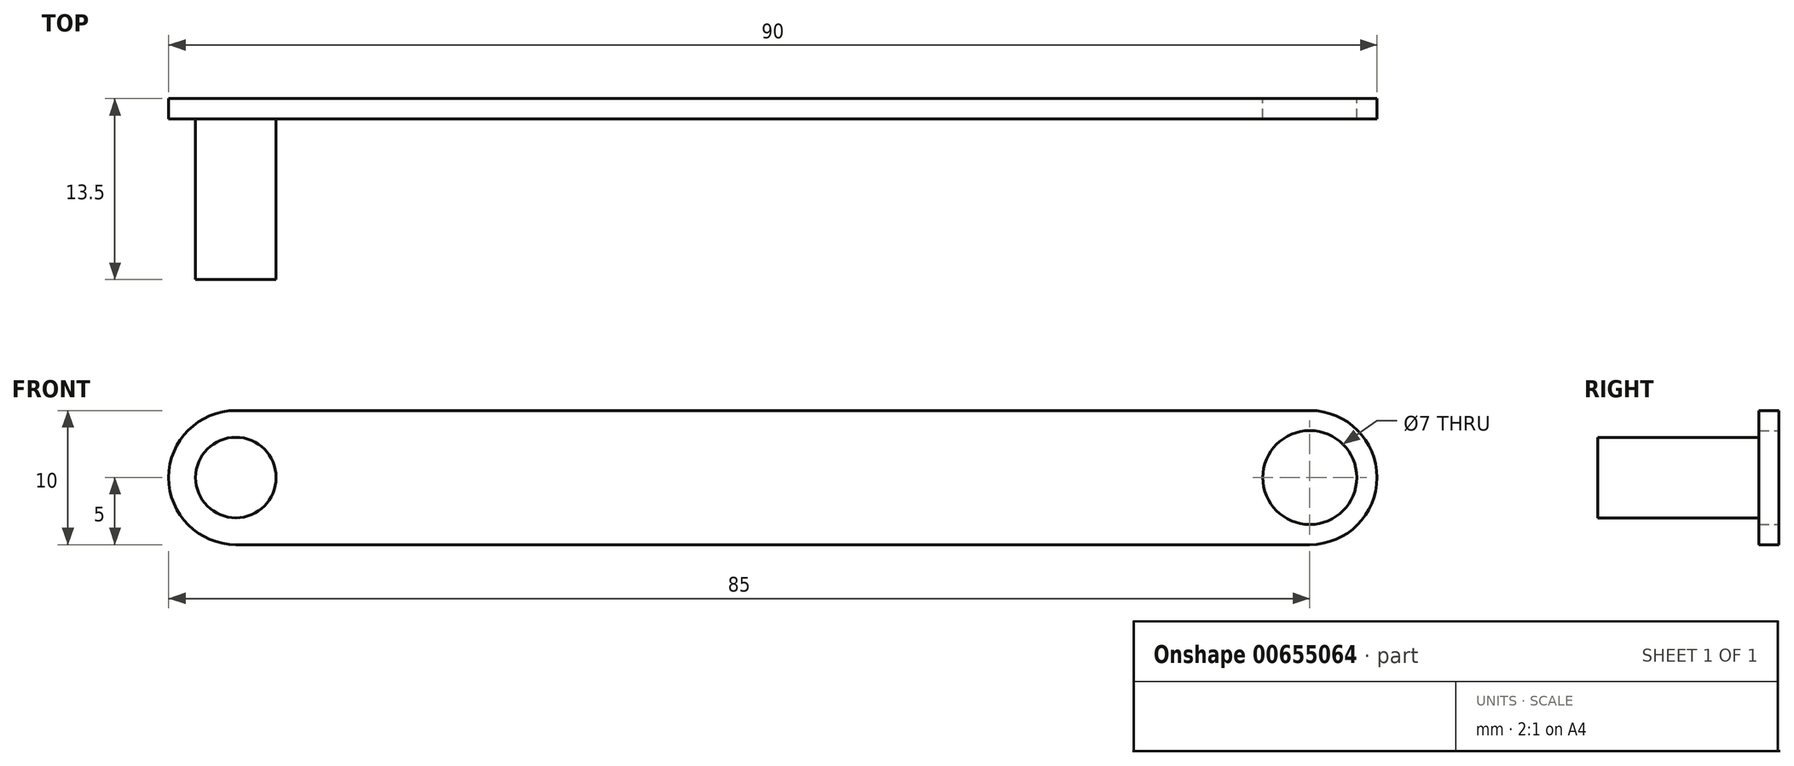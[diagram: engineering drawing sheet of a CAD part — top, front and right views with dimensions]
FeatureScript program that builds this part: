
annotation { "Feature Type Name" : "Feature", "Feature Type Description" : "" }
export const myFeature = defineFeature(function(context is Context, id is Id, definition is map)
    precondition{}
    {
        {
            var Q0;
            Q0=qCreatedBy(makeId("Front.planeOp"),FACE);
            var sketch = newSketch(context, id + "F0", { "sketchPlane" : qUnion([Q0])});
            skArc(sketch, "E0", {"start": v(0, 5) * mm, "mid": v(-5, 0) * mm, "end": v(0, -5) * mm});
            skArc(sketch, "E1.1.0.0", {"start": v(80, -5) * mm, "mid": v(85, 0) * mm, "end": v(80, 5) * mm});
            skCircle(sketch, "E1.1.0.1", {"center": v(80, 0) * mm, "radius": 3.5 * mm});
            skLineSegment(sketch, "E2", {"start": v(0, 5) * mm, "end": v(80, 5) * mm});
            skLineSegment(sketch, "E3", {"start": v(0, -5) * mm, "end": v(80, -5) * mm});
            skSolve(sketch);
        }
        {
            var Q0;
            Q0 = qSketchRegion(id + "F0", true);
            extrude(context, id + "F1", {"entities" : qUnion([Q0]), "depth" : 1.5 * mm, "offsetDistance" : 25 * mm});
        }
        {
            var Q0;
            Q0=makeQuery(id+"F1.opExtrude","CAP_FACE",FACE,{"disambiguationData":[OSD([sQuery(id+"F0.wireOp",EDGE,"E0"),sQuery(id+"F0.wireOp",EDGE,"E1.1.0.0"),sQuery(id+"F0.wireOp",EDGE,"E1.1.0.1"),sQuery(id+"F0.wireOp",EDGE,"E2"),sQuery(id+"F0.wireOp",EDGE,"E3")])],"isStart":false});
            var sketch = newSketch(context, id + "F2", { "sketchPlane" : qUnion([Q0])});
            skCircle(sketch, "E4", {"center": v(0, 0) * mm, "radius": 3 * mm});
            skSolve(sketch);
        }
        {
            var Q0;
            Q0 = qSketchRegion(id + "F2", true);
            extrude(context, id + "F3", {"entities" : qUnion([Q0]), "operationType" : NewBodyOperationType.ADD, "depth" : 12 * mm, "offsetDistance" : 25 * mm});
        }
    });
